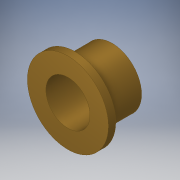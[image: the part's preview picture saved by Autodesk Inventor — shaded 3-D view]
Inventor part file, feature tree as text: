
AUTODESK INVENTOR PART (.ipt)
format: ipt  version: 2019.4 (Build 234330000, 330)  size: 114,688 bytes
history: native  units: in
note: dims shown in document units (in); Inventor stores cm internally (conversion verified against a paired STEP export)
features: extrude x2, sketch x2, projected_geometry x1
ambient origin geometry x8: Origin, YZ Plane, XZ Plane, XY Plane, X Axis, Y Axis, Z Axis, Center Point
bodies: Solid1 (feature_tree)
feature tree (5):
  extrude  "Extrusion1"  Depth=0.375in
  extrude  "Extrusion2"  Depth=0.0625in
  sketch  "Sketch1"  dims[d0=0.501in d1=0.375in]
  sketch  "Sketch2"  dims[d2=0.375in d3=0.0in d4=0.688in d5=0.0625in d6=0.0in]
  projected_geometry  "Projected Loop1"
